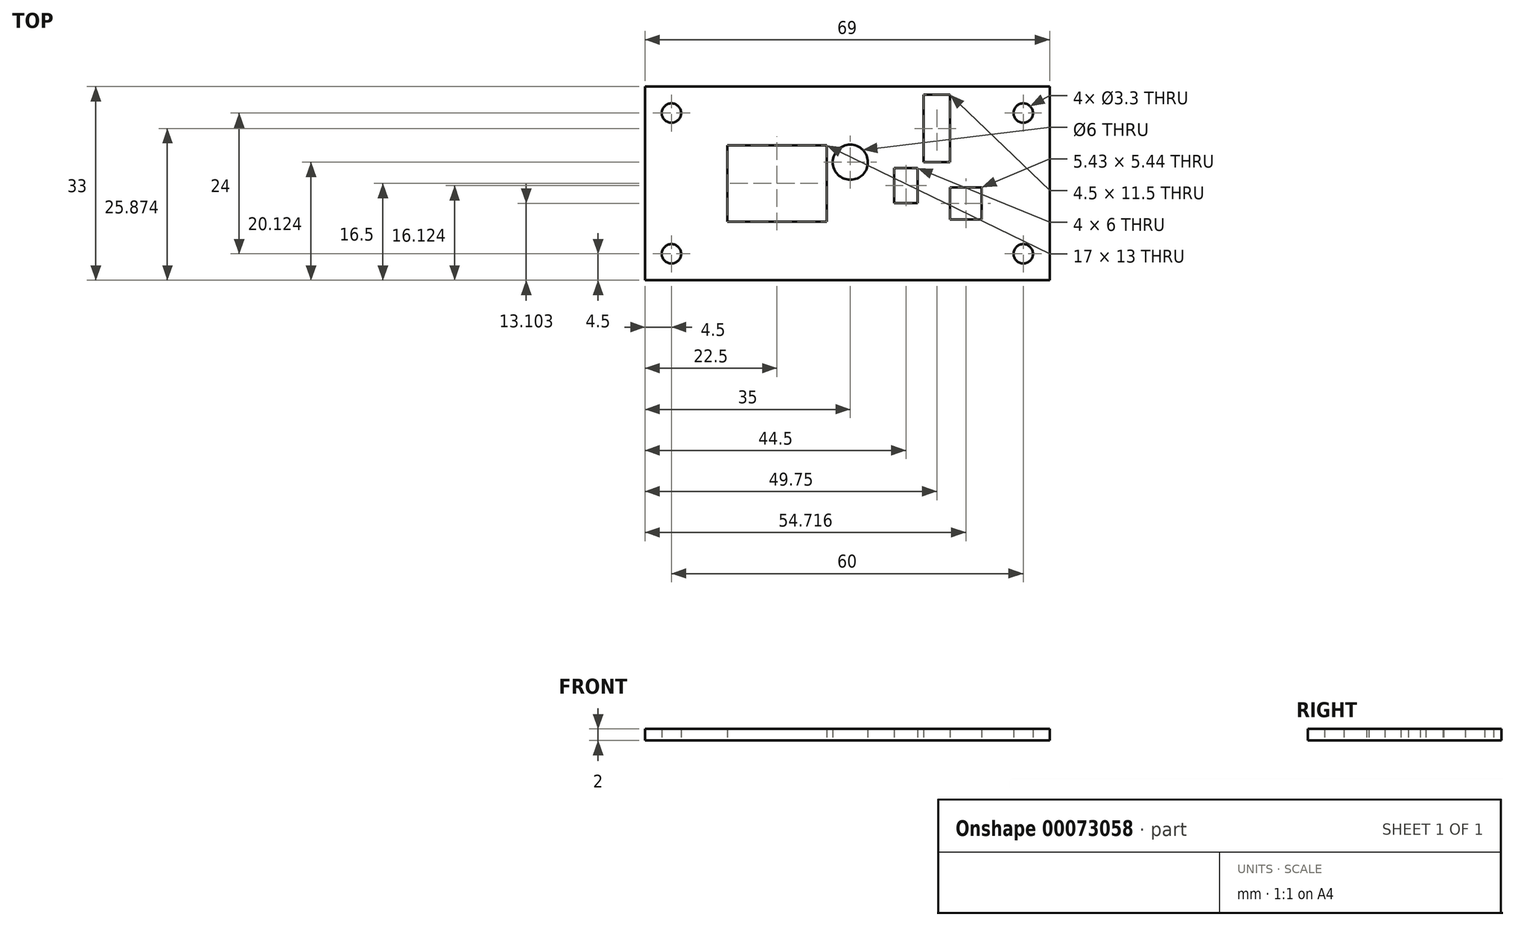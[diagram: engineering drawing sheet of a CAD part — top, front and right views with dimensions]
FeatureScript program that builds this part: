
annotation { "Feature Type Name" : "Feature", "Feature Type Description" : "" }
export const myFeature = defineFeature(function(context is Context, id is Id, definition is map)
    precondition{}
    {
        {
            var Q0;
            Q0=qCreatedBy(makeId("Top.planeOp"),FACE);
            var sketch = newSketch(context, id + "F0", { "sketchPlane" : qUnion([Q0])});
            skLineSegment(sketch, "E0.bottom", {"start": v(0, 0) * mm, "end": v(69, 0) * mm});
            skLineSegment(sketch, "E0.top", {"start": v(0, -33) * mm, "end": v(69, -33) * mm});
            skLineSegment(sketch, "E0.left", {"start": v(0, 0) * mm, "end": v(0, -33) * mm});
            skLineSegment(sketch, "E0.right", {"start": v(69, 0) * mm, "end": v(69, -33) * mm});
            skLineSegment(sketch, "E1", {"start": v(78.24, -4.5) * mm, "end": v(-6.53, -4.5) * mm, "construction": true});
            skLineSegment(sketch, "E2", {"start": v(79.5, -28.5) * mm, "end": v(-5.75, -28.5) * mm, "construction": true});
            skLineSegment(sketch, "E3", {"start": v(64.5, -38.48) * mm, "end": v(64.5, 5.9) * mm, "construction": true});
            skLineSegment(sketch, "E4", {"start": v(4.5, 4.64) * mm, "end": v(4.5, -40.13) * mm, "construction": true});
            skCircle(sketch, "E5", {"center": v(4.5, -4.5) * mm, "radius": 1.65 * mm});
            skCircle(sketch, "E6", {"center": v(4.5, -28.5) * mm, "radius": 1.65 * mm});
            skCircle(sketch, "E7", {"center": v(64.5, -4.5) * mm, "radius": 1.65 * mm});
            skCircle(sketch, "E8", {"center": v(64.5, -28.5) * mm, "radius": 1.65 * mm});
            skLineSegment(sketch, "E9.bottom", {"start": v(14, -10) * mm, "end": v(31, -10) * mm});
            skLineSegment(sketch, "E9.top", {"start": v(14, -23) * mm, "end": v(31, -23) * mm});
            skLineSegment(sketch, "E9.left", {"start": v(14, -10) * mm, "end": v(14, -23) * mm});
            skLineSegment(sketch, "E9.right", {"start": v(31, -10) * mm, "end": v(31, -23) * mm});
            skLineSegment(sketch, "E10", {"start": v(31, -16.5) * mm, "end": v(0, -16.5) * mm, "construction": true});
            skPoint(sketch, "E10.endSnap0", {"position": v(14, -16.5) * mm});
            skCircle(sketch, "E11", {"center": v(35, -12.88) * mm, "radius": 3 * mm});
            skLineSegment(sketch, "E12.bottom", {"start": v(42.5, -13.88) * mm, "end": v(46.5, -13.88) * mm});
            skLineSegment(sketch, "E12.top", {"start": v(42.5, -19.88) * mm, "end": v(46.5, -19.88) * mm});
            skLineSegment(sketch, "E12.left", {"start": v(42.5, -13.88) * mm, "end": v(42.5, -19.88) * mm});
            skLineSegment(sketch, "E12.right", {"start": v(46.5, -13.88) * mm, "end": v(46.5, -19.88) * mm});
            skLineSegment(sketch, "E13.bottom", {"start": v(47.5, -1.38) * mm, "end": v(52, -1.38) * mm});
            skLineSegment(sketch, "E13.top", {"start": v(47.5, -12.88) * mm, "end": v(52, -12.88) * mm});
            skLineSegment(sketch, "E13.left", {"start": v(47.5, -1.38) * mm, "end": v(47.5, -12.88) * mm});
            skLineSegment(sketch, "E13.right", {"start": v(52, -1.38) * mm, "end": v(52, -12.88) * mm});
            skLineSegment(sketch, "E14.bottom", {"start": v(52, -17.18) * mm, "end": v(57.43, -17.18) * mm});
            skLineSegment(sketch, "E14.top", {"start": v(52, -22.62) * mm, "end": v(57.43, -22.62) * mm});
            skLineSegment(sketch, "E14.left", {"start": v(52, -17.18) * mm, "end": v(52, -22.62) * mm});
            skLineSegment(sketch, "E14.right", {"start": v(57.43, -17.18) * mm, "end": v(57.43, -22.62) * mm});
            skSolve(sketch);
        }
        {
            var Q0;
            Q0 = qSketchRegion(id + "F0", true);
            extrude(context, id + "F1", {"entities" : qUnion([Q0]), "depth" : 2 * mm});
        }
    });
